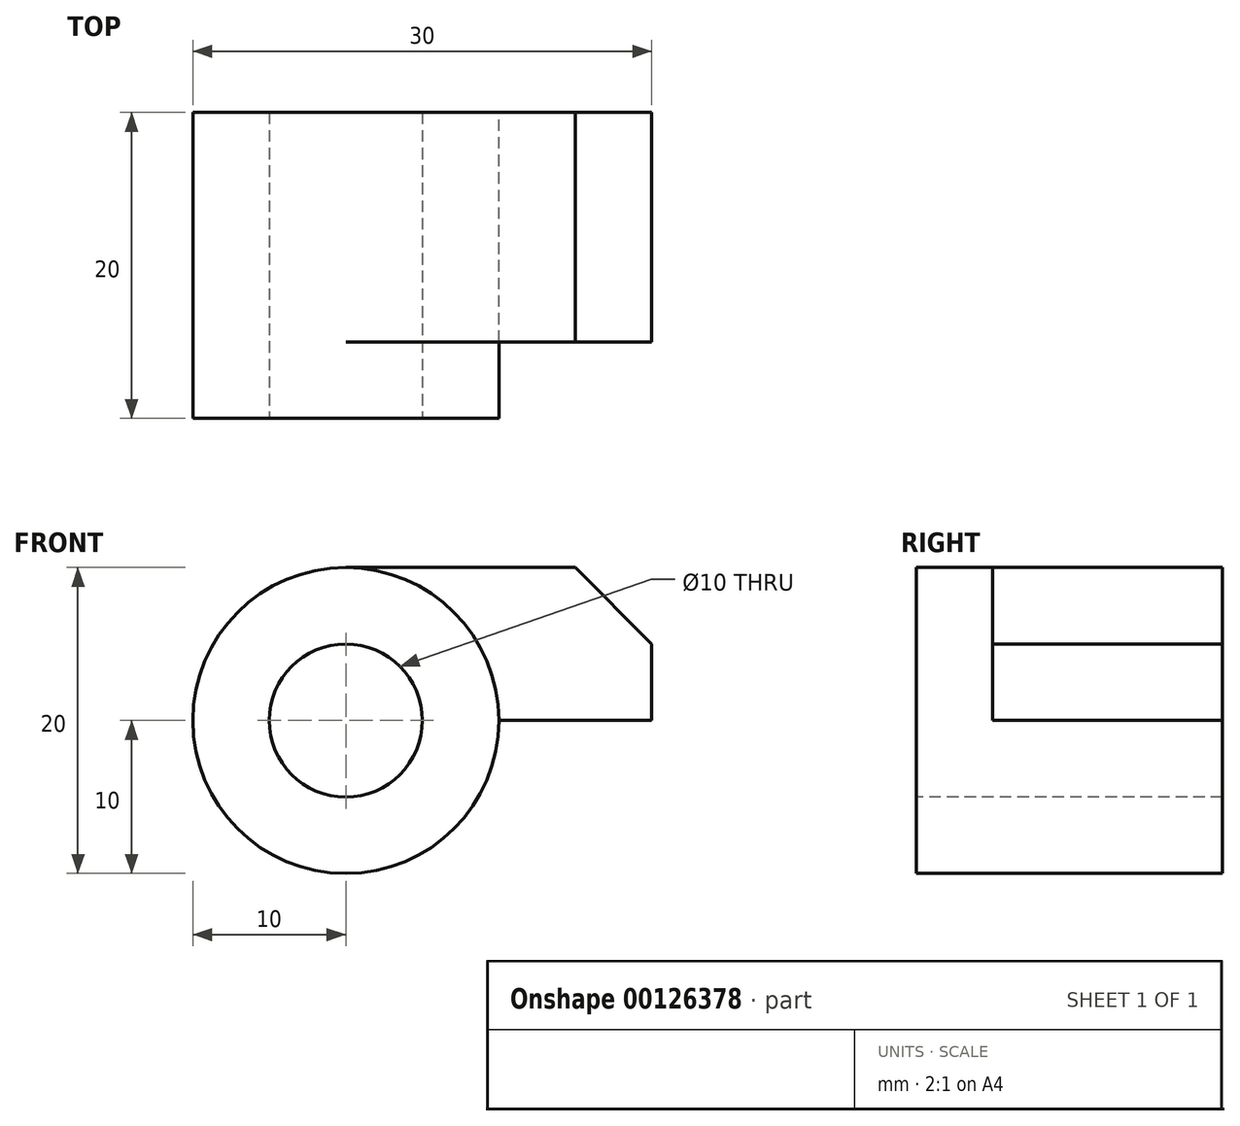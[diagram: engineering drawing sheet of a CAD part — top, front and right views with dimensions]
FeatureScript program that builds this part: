
annotation { "Feature Type Name" : "Feature", "Feature Type Description" : "" }
export const myFeature = defineFeature(function(context is Context, id is Id, definition is map)
    precondition{}
    {
        {
            var Q0;
            Q0=qCreatedBy(makeId("Front.planeOp"),FACE);
            var sketch = newSketch(context, id + "F0", { "sketchPlane" : qUnion([Q0])});
            skCircle(sketch, "E0", {"center": v(0, 0) * mm, "radius": 5 * mm});
            skCircle(sketch, "E1", {"center": v(0, 0) * mm, "radius": 10 * mm});
            skSolve(sketch);
        }
        {
            var Q0;
            Q0=makeQuery(id+"F0.imprint","IMPRINT",FACE,{"disambiguationData":[TD([[makeQuery(id+"F0.imprint","IMPRINT",EDGE,{"derivedFrom":sQuery(id+"F0.wireOp",EDGE,"E0")}),-1.0]])]});
            extrude(context, id + "F1", {"entities" : qUnion([Q0]), "oppositeDirection" : true, "depth" : 20 * mm});
        }
        {
            var Q0;
            Q0=makeQuery(id+"F1.opExtrude","CAP_FACE",FACE,{"disambiguationData":[OSD([sQuery(id+"F0.wireOp",EDGE,"E0"),sQuery(id+"F0.wireOp",EDGE,"E1")])],"isStart":false});
            var sketch = newSketch(context, id + "F2", { "sketchPlane" : qUnion([Q0])});
            skLineSegment(sketch, "E2", {"start": v(-20, 5) * mm, "end": v(-20, 0) * mm});
            skLineSegment(sketch, "E3", {"start": v(-20, 0) * mm, "end": v(-10, 0) * mm});
            skArc(sketch, "E4", {"start": v(0, 10) * mm, "mid": v(-7.07, 7.07) * mm, "end": v(-10, 0) * mm});
            skLineSegment(sketch, "E5", {"start": v(0, 10) * mm, "end": v(-15, 10) * mm});
            skLineSegment(sketch, "E6", {"start": v(-20, 5) * mm, "end": v(-15, 10) * mm});
            skSolve(sketch);
        }
        {
            var Q0;
            Q0 = qSketchRegion(id + "F2", true);
            extrude(context, id + "F3", {"entities" : qUnion([Q0]), "operationType" : NewBodyOperationType.ADD, "oppositeDirection" : true, "depth" : 15 * mm});
        }
    });
